# Revit family: LED-600_4500lum_UGR_2021_11_03
name_source: partatom
category: Leuchten
units: mm (PartAtom-declared; Revit-internal decimal feet)

## family parameters
Basisbauteil = Decke
Beim Laden mit Abzugskörper schneiden = Nein
Bemaßung runder Anschluss = Durchmesser verwenden
Gemeinsam genutzt = Nein
Immer vertikal = Ja
Lichtquelle = Ja
OmniClass-Nummer = 23.80.70.11
OmniClass-Titel = Luminaries for Internal Lighting
Raumberechnungspunkt = Nein
Teiletyp = Normal

## types (11) — shared parameters
Beschreibung = Clean Room Light
Datei für fotometrisches Netz = ISO-U3 600 4.5 AG.ies
Farbfilter = 16777215
Farbtemperaturverschiebung bei Dämpfen der Lampe = <Keine Auswahl>
Hersteller = Lindner Group
LIN_A_4_Cable Entry = 2x cable gland M16 on the back
LIN_A_4_Ceiling Installation Detail = recessed
LIN_A_4_Cover Material = thoughened safty glas clear
LIN_A_4_Lighting Fixture Body Color = RAL 9016
LIN_A_4_Safty Class = 1
LIN_A_4_Through Wiring = Yes
LIN_A_5_Ceiling Installation Detail = recessed
LIN_A_8_Colour Tolerance = <=3 SDCM
LIN_A_8_Protection Degree = IP65 on the room side, IP50 to the ceiling
LIN_A_8_Safty Class = 1
LIN_A_8_UGR = UGR<19
LIN_E_4_Num of Lighting Sources = 4
LIN_E_8_Standby Power = 0 W
LIN_E_8_System Power = 31 W
LIN_E_8_Voltage Rage = 220-240V
Lampe = LED
Neigungswinkel = 60.00°
Scheinlast = 31 VA
Typenbild = rrt_tu_leuchten_cp-4-lichteinheiten_00.png
URL = https://www.lindner-group.com
Von Linienlänge aussenden = 542 mm  [stored 1.77822 ft]

## per-type parameters (varying)
| type | LIN_A_4_Connection Type | LIN_A_4_Emergency Light Function | LIN_A_4_Material Light Diffuser | LIN_A_4_Material Lighting Fixture Body | LIN_A_5_Lindner Model Name | LIN_A_8_Color Rendering Index | LIN_E_4_Ballast | LIN_E_8_Frequency | LIN_E_8_Max ECG no. in Circuit Breacker | Modell | Typenkommentare |
| Standart | 3-pole terminal block | No | <Nach Kategorie> | <Nach Kategorie> | CP 600 LED-U3 4.5 AG | >=80 | Electronic ballast (switchable) | 50/60Hz | B16 - max.16 | ISO-U3 600 4.5 AG | No added functions |
| Em Light | 3-pole terminal block | Yes | <Nach Kategorie> | <Nach Kategorie> | CP 600 LED-U3 4.5 AG NL | >=80 | Electronic ballast (switchable) | 0/50/60Hz | B16 - max.16 | ISO-U3 600 4.5 AG NL | Emergency Light Function |
| Dimming | 5-pole terminal block | No | <Nach Kategorie> | <Nach Kategorie> | CP 600 LED-U3 4.5 AG DA | >=80 | Electronic ballast (DALI-dimmable) | 50/60Hz | B16 - max.21 | ISO-U3 600 4.5 AG DA | Dimming Function |
| Em Light_Dimming | 5-pole terminal block | Yes | <Nach Kategorie> | <Nach Kategorie> | CP 600 LED-U3 4.5 AG CRI DA | >=80 | Electronic ballast (DALI-dimmable) | 0/50/60Hz | B16 - max.21 | ISO-U3 600 4.5 AG CRI DA | Emergency Light Function; Dimming Function |
| High CRI | 3-pole terminal block | No | <Nach Kategorie> | <Nach Kategorie> | CP 600 LED-U3 4.5 AG CRI | >=90 | Electronic ballast (switchable) | 50/60Hz | B16 - max.16 | ISO-U3 600 4.5 AG CRI | CRI >=90 |
| Hight CRI_Dimming | 5-pole terminal block | No | <Nach Kategorie> | <Nach Kategorie> | CP 600 LED-U3 4.5 AG NL | >=90 | Electronic ballast (DALI-dimmable) | 50/60Hz | B16 - max.21 | ISO-U3 600 4.5 AG NL | CRI >=90; Dimming Function |
| High CRI_Dimming_Em Light | 5-pole terminal block | Yes | <Nach Kategorie> | <Nach Kategorie> | CP 600 LED-U3 4.5 AG CRI DA NL | >=90 | Electronic ballast (DALI-dimmable) | 0/50/60Hz | B16 - max.21 | ISO-U3 600 4.5 AG CRI DA NL | CRI >=90; Dimming Function; Emergency Light Function |
| 6500K | 3-pole terminal block | No | Glass, Thoughened Clear | Steel Sheet | CP 600 LED-U3 4.5 AG 6500K | >=80 | Electronic ballast (switchable) | 50/60Hz | B16 - max.16 | ISO-U3 600 4.5 AG 6500K | Color 6500k |
| 6500K_Dimming | 5-pole terminal block | No | <Nach Kategorie> | <Nach Kategorie> | CP 600 LED-U3 4.5 AG 6500K DA | >=80 | Electronic ballast (DALI-dimmable) | 50/60Hz | B16 - max.21 | ISO-U3 600 4.5 AG 6500K DA | Color 6500k; Dimming Function |
| 6500K_Em Light_Dimming | 5-pole terminal block | Yes | <Nach Kategorie> | <Nach Kategorie> | CP 600 LED-U3 4.5 AG 6500K DA NL | >=80 | Electronic ballast (DALI-dimmable) | 0/50/60Hz | B16 - max.21 | ISO-U3 600 4.5 AG 6500K DA NL | Color 6500k; Emergency Light Function; Dimming Function |
| 6500K_Em Light_Dimming_High CRI | 5-pole terminal block | Yes | <Nach Kategorie> | <Nach Kategorie> | CP 600 LED-U3 4.5 AG 6500K CRI DA NL | >=90 | Electronic ballast (DALI-dimmable) | 0/50/60Hz | B16 - max.21 | ISO-U3 600 4.5 AG 6500K CRI DA NL | Color 6500k; Emergency Light Function; Dimming Function; CRI >= 90 |

note: [stored X ft] marks values corroborated as IEEE doubles in the binary element streams (Revit-internal decimal feet)

## geometry (parser evidence)
native form markers: Sweep x4
no freeform markers — native parametric forms only
